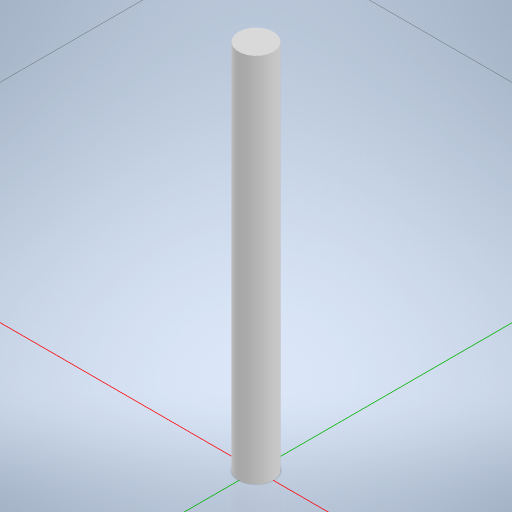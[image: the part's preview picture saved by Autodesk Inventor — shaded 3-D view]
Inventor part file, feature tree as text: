
AUTODESK INVENTOR PART (.ipt)
format: ipt  version: 2024 (Build 280153000, 153)  size: 229,376 bytes
history: native  units: mm
features: extrude x1, sketch x1
ambient origin geometry x8: Origin, YZ Plane, XZ Plane, XY Plane, X Axis, Y Axis, Z Axis, Center Point
bodies: Volumenkörper1 (feature_tree)
feature tree (2):
  extrude  "Extrusion1"  Depth=16.0mm TaperAngle=0.0deg
  sketch  "Skizze1"  dims[d0=1.5mm d1=16.0mm d2=0.0mm]
